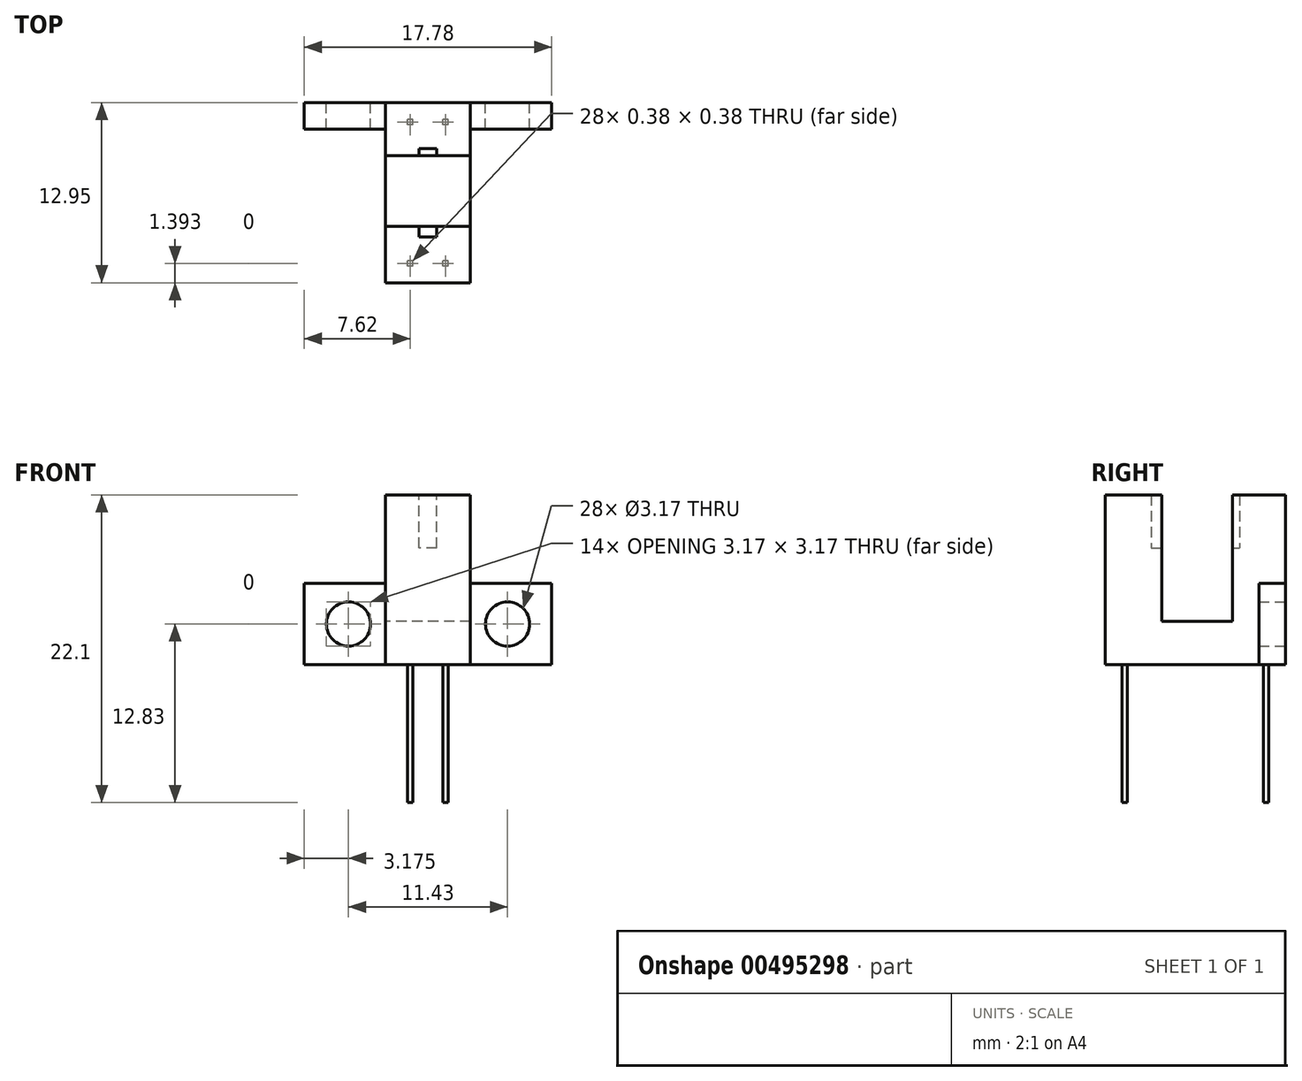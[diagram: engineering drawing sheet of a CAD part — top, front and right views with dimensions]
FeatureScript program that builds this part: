
annotation { "Feature Type Name" : "Feature", "Feature Type Description" : "" }
export const myFeature = defineFeature(function(context is Context, id is Id, definition is map)
    precondition{}
    {
        {
            var Q0;
            Q0=qCreatedBy(makeId("Front.planeOp"),FACE);
            var sketch = newSketch(context, id + "F0", { "sketchPlane" : qUnion([Q0])});
            skLineSegment(sketch, "E0", {"start": v(-8.9, -2.92) * mm, "end": v(8.9, -2.92) * mm});
            skLineSegment(sketch, "E1", {"start": v(8.9, -2.92) * mm, "end": v(8.9, 2.92) * mm});
            skLineSegment(sketch, "E2", {"start": v(8.9, 2.92) * mm, "end": v(3.05, 2.92) * mm});
            skLineSegment(sketch, "E3", {"start": v(3.05, 2.92) * mm, "end": v(3.05, 9.27) * mm});
            skLineSegment(sketch, "E4", {"start": v(3.05, 9.27) * mm, "end": v(-3.05, 9.27) * mm});
            skLineSegment(sketch, "E5", {"start": v(-3.05, 9.27) * mm, "end": v(-3.05, 2.92) * mm});
            skLineSegment(sketch, "E6", {"start": v(-3.05, 2.92) * mm, "end": v(-8.9, 2.92) * mm});
            skLineSegment(sketch, "E7", {"start": v(-8.9, 2.92) * mm, "end": v(-8.9, -2.92) * mm});
            skCircle(sketch, "E8", {"center": v(5.72, 0) * mm, "radius": 1.59 * mm});
            skCircle(sketch, "E9", {"center": v(-5.72, 0) * mm, "radius": 1.59 * mm});
            skPoint(sketch, "E10", {"position": v(-8.9, 0) * mm});
            skPoint(sketch, "E11", {"position": v(0, -2.92) * mm});
            skLineSegment(sketch, "E12", {"start": v(-5.72, 0) * mm, "end": v(5.72, 0) * mm, "construction": true});
            skPoint(sketch, "E13", {"position": v(0, 0) * mm});
            skLineSegment(sketch, "E14", {"start": v(-1.46, -2.92) * mm, "end": v(-1.46, -12.83) * mm});
            skLineSegment(sketch, "E15", {"start": v(-1.46, -12.83) * mm, "end": v(-1.08, -12.83) * mm});
            skLineSegment(sketch, "E16", {"start": v(-1.08, -12.83) * mm, "end": v(-1.08, -2.92) * mm});
            skLineSegment(sketch, "E17", {"start": v(1.08, -2.92) * mm, "end": v(1.08, -12.83) * mm});
            skLineSegment(sketch, "E18", {"start": v(1.08, -12.83) * mm, "end": v(1.46, -12.83) * mm});
            skLineSegment(sketch, "E19", {"start": v(1.46, -12.83) * mm, "end": v(1.46, -2.92) * mm});
            skLineSegment(sketch, "E20", {"start": v(-1.08, -12.83) * mm, "end": v(1.08, -12.83) * mm, "construction": true});
            skPoint(sketch, "E21", {"position": v(0, -12.83) * mm});
            skSolve(sketch);
        }
        {
            var Q0;
            Q0 = qSketchRegion(id + "F0", true);
            extrude(context, id + "F1", {"entities" : qUnion([Q0]), "endBound" : BoundingType.SYMMETRIC, "depth" : 254 * mm});
        }
        {
            var Q0;
            Q0=qCreatedBy(makeId("Right.planeOp"),FACE);
            var sketch = newSketch(context, id + "F2", { "sketchPlane" : qUnion([Q0])});
            skLineSegment(sketch, "E22", {"start": v(-12.95, 9.27) * mm, "end": v(-12.95, -2.92) * mm});
            skLineSegment(sketch, "E23", {"start": v(-12.95, -2.92) * mm, "end": v(0, -2.92) * mm});
            skLineSegment(sketch, "E24", {"start": v(0, -2.92) * mm, "end": v(0, 9.27) * mm});
            skLineSegment(sketch, "E25", {"start": v(0, 9.27) * mm, "end": v(-3.81, 9.27) * mm});
            skLineSegment(sketch, "E26", {"start": v(-3.81, 9.27) * mm, "end": v(-3.8, 0.18) * mm});
            skLineSegment(sketch, "E27", {"start": v(-3.8, 0.18) * mm, "end": v(-8.9, 0.18) * mm});
            skLineSegment(sketch, "E28", {"start": v(-8.89, 0.18) * mm, "end": v(-8.89, 9.27) * mm});
            skLineSegment(sketch, "E29", {"start": v(-8.89, 9.27) * mm, "end": v(-12.95, 9.27) * mm});
            skLineSegment(sketch, "E30", {"start": v(-11.75, -2.92) * mm, "end": v(-11.75, -12.83) * mm});
            skLineSegment(sketch, "E31", {"start": v(-11.75, -12.83) * mm, "end": v(-11.37, -12.83) * mm});
            skLineSegment(sketch, "E32", {"start": v(-11.37, -12.83) * mm, "end": v(-11.37, -2.92) * mm});
            skLineSegment(sketch, "E33", {"start": v(-1.59, -2.92) * mm, "end": v(-1.59, -12.83) * mm});
            skLineSegment(sketch, "E34", {"start": v(-1.59, -12.83) * mm, "end": v(-1.2, -12.83) * mm});
            skLineSegment(sketch, "E35", {"start": v(-1.2, -12.83) * mm, "end": v(-1.2, -2.92) * mm});
            skLineSegment(sketch, "E36", {"start": v(-11.37, -12.83) * mm, "end": v(-1.59, -12.83) * mm, "construction": true});
            skPoint(sketch, "E37", {"position": v(-6.48, -2.92) * mm});
            skPoint(sketch, "E38", {"position": v(-6.48, -12.83) * mm});
            skSolve(sketch);
        }
        {
            var Q0;
            {var subQ4=sQuery(id+"F2.wireOp",EDGE,"E22");Q0=makeQuery(id+"F2.imprint","IMPRINT",FACE,{"disambiguationData":[TD([[makeQuery(id+"F2.imprint","IMPRINT",EDGE,{"derivedFrom":subQ4}),1.0]])]});}
            var Q1;
            {var subQ0=sQuery(id+"F2.wireOp",EDGE,"E33");Q1=makeQuery(id+"F2.imprint","IMPRINT",FACE,{"disambiguationData":[TD([[makeQuery(id+"F2.imprint","IMPRINT",EDGE,{"derivedFrom":subQ0}),1.0]])]});}
            var Q2;
            {var subQ0=sQuery(id+"F2.wireOp",EDGE,"E30");Q2=makeQuery(id+"F2.imprint","IMPRINT",FACE,{"disambiguationData":[TD([[makeQuery(id+"F2.imprint","IMPRINT",EDGE,{"derivedFrom":subQ0}),1.0]])]});}
            extrude(context, id + "F3", {"entities" : qUnion([Q0, Q1, Q2]), "operationType" : NewBodyOperationType.INTERSECT, "endBound" : BoundingType.SYMMETRIC, "depth" : 254 * mm});
        }
        {
            var Q0;
            Q0=qCreatedBy(makeId("Front.planeOp"),FACE);
            var Q1;
            Q1=sQuery(id+"F2.wireOp",VERTEX,"E37");
            cPlane(context, id + "F4", {"entities" : qUnion([Q0, Q1]), "cplaneType" : CPlaneType.PLANE_POINT, "offset" : 25.4 * mm, "width" : 152.4 * mm, "height" : 152.4 * mm});
        }
        {
            var Q0;
            Q0=qCreatedBy(id+"F4.planeOp",FACE);
            var sketch = newSketch(context, id + "F5", { "sketchPlane" : qUnion([Q0])});
            skLineSegment(sketch, "E39.bottom", {"start": v(-0.64, 9.27) * mm, "end": v(0.64, 9.27) * mm});
            skLineSegment(sketch, "E39.top", {"start": v(-0.64, 5.46) * mm, "end": v(0.64, 5.46) * mm});
            skLineSegment(sketch, "E39.left", {"start": v(-0.64, 9.27) * mm, "end": v(-0.64, 5.46) * mm});
            skLineSegment(sketch, "E39.right", {"start": v(0.63, 9.27) * mm, "end": v(0.63, 5.46) * mm});
            skSolve(sketch);
        }
        {
            var Q0;
            Q0=qCreatedBy(makeId("Top.planeOp"),FACE);
            var sketch = newSketch(context, id + "F6", { "sketchPlane" : qUnion([Q0])});
            skLineSegment(sketch, "E40.0", {"start": v(-8.9, 0) * mm, "end": v(8.9, 0) * mm});
            skLineSegment(sketch, "E41", {"start": v(-8.9, 0) * mm, "end": v(-8.9, -1.9) * mm});
            skLineSegment(sketch, "E42", {"start": v(-8.9, -1.9) * mm, "end": v(-3.05, -1.9) * mm});
            skLineSegment(sketch, "E43", {"start": v(-3.05, -1.9) * mm, "end": v(-3.05, -12.95) * mm});
            skLineSegment(sketch, "E44", {"start": v(-3.05, -12.95) * mm, "end": v(3.05, -12.95) * mm});
            skLineSegment(sketch, "E45", {"start": v(3.05, -12.95) * mm, "end": v(3.05, -1.9) * mm});
            skLineSegment(sketch, "E46", {"start": v(3.05, -1.9) * mm, "end": v(8.9, -1.9) * mm});
            skLineSegment(sketch, "E47", {"start": v(8.89, -1.9) * mm, "end": v(8.89, 0) * mm});
            skSolve(sketch);
        }
        {
            var Q0;
            Q0=makeQuery(id+"F6.imprint","IMPRINT",FACE,{"disambiguationData":[TD([[makeQuery(id+"F6.imprint","IMPRINT",EDGE,{"derivedFrom":sQuery(id+"F6.wireOp",EDGE,"E40.0")}),-1.0]])]});
            extrude(context, id + "F7", {"entities" : qUnion([Q0]), "operationType" : NewBodyOperationType.INTERSECT, "endBound" : BoundingType.SYMMETRIC, "depth" : 254 * mm});
        }
        {
            var Q0;
            Q0=makeQuery(id+"F5.imprint","IMPRINT",FACE,{"disambiguationData":[TD([[makeQuery(id+"F5.imprint","IMPRINT",EDGE,{"derivedFrom":sQuery(id+"F5.wireOp",EDGE,"E39.bottom")}),-1.0]])]});
            extrude(context, id + "F8", {"entities" : qUnion([Q0]), "operationType" : NewBodyOperationType.REMOVE, "endBound" : BoundingType.SYMMETRIC, "depth" : 6.35 * mm});
        }
    });
